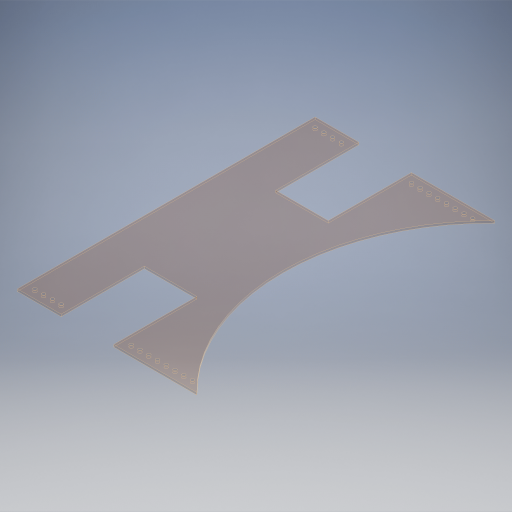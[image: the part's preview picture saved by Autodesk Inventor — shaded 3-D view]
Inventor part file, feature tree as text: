
AUTODESK INVENTOR PART (.ipt)
format: ipt  version: 2024.2 (Build 282272000, 272)  size: 378,880 bytes
history: native  units: in
note: dims shown in document units (in); Inventor stores cm internally (conversion verified against a paired STEP export)
features: extrude x2, sketch x2, projected_geometry x1
ambient origin geometry x8: Origin, YZ Plane, XZ Plane, XY Plane, X Axis, Y Axis, Z Axis, Center Point
bodies: Solid1 (feature_tree)
feature tree (5):
  extrude  "Extrusion1"  Depth=17.0in
  extrude  "Extrusion2"  Depth=4.75in
  sketch  "Sketch1"  dims[d0=23.748in d1=17.0in]
  sketch  "Sketch2"  dims[d2=2.5in d3=4.75in d4=3.0in d5=2.5in d6=4.75in d7=3.0in d8=4.75in d9=4.75in d10=0.196in d11=0.5in d12=0.5in d13=1.5748in d15=0.5in d16=0.3937in d18=1.0in d20=0.196in d21=0.5in d22=0.5in d23=3.1496in d25=0.5in d26=0.3937in d28=1.0in d30=0.5in d31=0.25in d32=0.0in d33=0.125in d34=0.0in]
  projected_geometry  "Projected Loop1"
